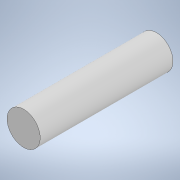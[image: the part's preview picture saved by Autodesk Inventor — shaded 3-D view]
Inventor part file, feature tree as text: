
AUTODESK INVENTOR PART (.ipt)
format: ipt  version: 2022 (Build 260153000, 153)  size: 92,672 bytes
history: native  units: in
note: dims shown in document units (in); Inventor stores cm internally (conversion verified against a paired STEP export)
features: revolve x1, sketch x1
ambient origin geometry x8: Origin, YZ Plane, XZ Plane, XY Plane, X Axis, Y Axis, Z Axis, Center Point
bodies: Solid1 (feature_tree)
feature tree (2):
  revolve  "Revolution1"  [1 undecoded]
  sketch  "Sketch1"  dims[d0=0.06in d1=0.015in d2=90.0deg]
note: 1 required parameter value undecoded (feature->parameter linkage not recoverable at this tier; creation-order binding heuristic only, values carry confidence <= 0.55)
